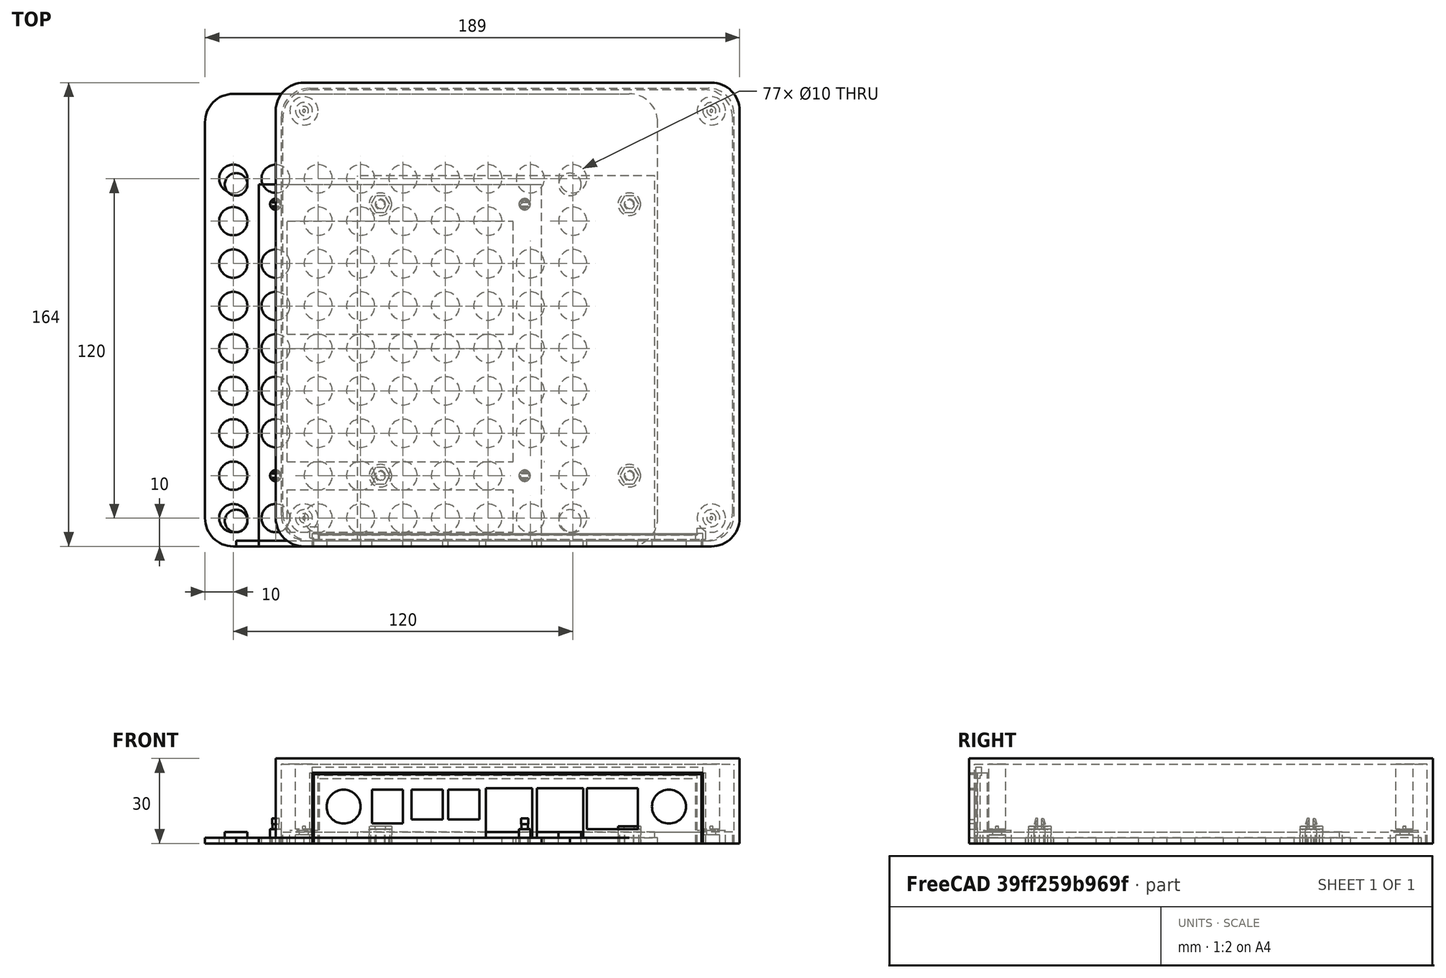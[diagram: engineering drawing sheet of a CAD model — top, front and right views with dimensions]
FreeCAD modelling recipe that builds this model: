
FCSTD DOCUMENT  (FreeCAD 0.16R6712 (Git))
Label: simple-case
License: All rights reserved
LicenseURL: http://en.wikipedia.org/wiki/All_rights_reserved
objects: Part::Fuse×53, Part::Cylinder×48, Part::Box×41, Part::Cut×27, PartDesign::Fillet×18, Part::FeaturePython×9, Part::Cone×4, Part::MultiCommon×4, Mesh::Feature×1, Sketcher::SketchObject×1, PartDesign::Pad×1
note: 207 computed .brp shape members not serialized (recipe doc carries the construction recipe); baked Part::Feature solids carry a one-line shape summary decoded from their .brp

FEATURE [PartDesign::Fillet] Fillet003
  Radius = 10
FEATURE [PartDesign::Fillet] Fillet007
  Placement = pos=(2,2,2) rot=(0,0,1;0rad)
  Radius = 9
FEATURE [Part::Cut] Cut
  Base = -> Fillet003
  Placement = pos=(-25,0,0) rot=(0,0,1;0rad)
  Tool = -> Fillet007
FEATURE [Part::Box] Box002  label="Ethernet"
  Height = 14.5
  Length = 18
  Placement = pos=(-1,0,-0.5) rot=(0,0,1;0rad)
  Width = 14.5
FEATURE [Part::Box] Box003  label="USB1"
  Height = 17.5
  Length = 16.4
  Placement = pos=(18.3,0,-0.5) rot=(0,0,1;0rad)
  Width = 10
FEATURE [Part::Box] Box004  label="USB2"
  Height = 17.5
  Length = 16.4
  Placement = pos=(36.3,0,-0.5) rot=(0,0,1;0rad)
  Width = 10
FEATURE [Part::Box] Box005  label="SPDIF1"
  Height = 10.5
  Length = 11
  Placement = pos=(55,0,0) rot=(0,0,1;0rad)
  Width = 10
FEATURE [Part::Box] Box006  label="SPDIF2"
  Height = 10.5
  Length = 11
  Placement = pos=(68,0,0) rot=(0,0,1;0rad)
  Width = 10
FEATURE [Part::Box] Box007  label="Power"
  Height = 12
  Length = 11
  Placement = pos=(82,0,0) rot=(0,0,1;0rad)
  Width = 10
FEATURE [Part::Fuse] Fusion
  Base = -> Box002
  Tool = -> Box003
FEATURE [Part::Fuse] Fusion001
  Base = -> Box007
  Tool = -> Fusion
FEATURE [Part::Fuse] Fusion002
  Base = -> Box006
  Tool = -> Fusion001
FEATURE [Part::Fuse] Fusion003
  Base = -> Box005
  Tool = -> Fusion002
FEATURE [Part::Fuse] Fusion004  label="Cutouts"
  Base = -> Box004
  Placement = pos=(90,-2,17) rot=(0,1,0;3.14159rad)
  Tool = -> Fusion003
FEATURE [Part::Cylinder] Cylinder  label="Zylinder"
  Angle = 360
  Height = 2
  Radius = 2
FEATURE [Part::Cylinder] Cylinder001  label="Zylinder001"
  Angle = 360
  Height = 3.8
  Radius = 1.3
FEATURE [Part::Cone] Cone  label="Kegel"
  Angle = 360
  Height = 2
  Placement = pos=(0,0,3.8) rot=(0,0,1;0rad)
  Radius1 = 2
  Radius2 = 1.4
FEATURE [Part::Box] Box008  label="Würfel008"
  Height = 4
  Length = 2.6
  Placement = pos=(-1.3,-5,3) rot=(0,0,1;0rad)
  Width = 10
FEATURE [Part::MultiCommon] Common
  Shapes = -> [Cone,Box008]
FEATURE [Part::Fuse] Fusion005
  Base = -> Cylinder
  Tool = -> Cylinder001
FEATURE [Part::Fuse] Fusion006
  Base = -> Common
  Tool = -> Fusion005
FEATURE [Part::Box] Box009  label="Würfel009"
  Height = 10
  Length = 10
  Placement = pos=(-3,-0.7,2) rot=(0,0,1;0rad)
  Width = 1.4
FEATURE [Part::Cut] Cut001
  Base = -> Fusion006
  Placement = pos=(0,23,0) rot=(0,0,1;0rad)
  Tool = -> Box009
FEATURE [Part::Cylinder] Cylinder002  label="Zylinder002"
  Angle = 360
  Height = 2
  Radius = 2
FEATURE [Part::Cylinder] Cylinder003  label="Zylinder003"
  Angle = 360
  Height = 3.8
  Radius = 1.3
FEATURE [Part::Cone] Cone001  label="Kegel001"
  Angle = 360
  Height = 2
  Placement = pos=(0,0,3.8) rot=(0,0,1;0rad)
  Radius1 = 2
  Radius2 = 1.4
FEATURE [Part::Box] Box010  label="Würfel010"
  Height = 4
  Length = 2.6
  Placement = pos=(-1.3,-5,3) rot=(0,0,1;0rad)
  Width = 10
FEATURE [Part::MultiCommon] Common001
  Shapes = -> [Cone001,Box010]
FEATURE [Part::Fuse] Fusion007
  Base = -> Cylinder002
  Tool = -> Cylinder003
FEATURE [Part::Fuse] Fusion008
  Base = -> Common001
  Tool = -> Fusion007
FEATURE [Part::Box] Box011  label="Würfel011"
  Height = 10
  Length = 10
  Placement = pos=(-3,-0.7,2) rot=(0,0,1;0rad)
  Width = 1.4
FEATURE [Part::Cut] Cut002
  Base = -> Fusion008
  Placement = pos=(0,119,0) rot=(0,0,1;0rad)
  Tool = -> Box011
FEATURE [Part::Cylinder] Cylinder004  label="Zylinder004"
  Angle = 360
  Height = 2
  Radius = 2
FEATURE [Part::Cylinder] Cylinder005  label="Zylinder005"
  Angle = 360
  Height = 3.8
  Radius = 1.3
FEATURE [Part::Cone] Cone002  label="Kegel002"
  Angle = 360
  Height = 2
  Placement = pos=(0,0,3.8) rot=(0,0,1;0rad)
  Radius1 = 2
  Radius2 = 1.4
FEATURE [Part::Box] Box012  label="Würfel012"
  Height = 4
  Length = 2.6
  Placement = pos=(-1.3,-5,3) rot=(0,0,1;0rad)
  Width = 10
FEATURE [Part::MultiCommon] Common002
  Shapes = -> [Cone002,Box012]
FEATURE [Part::Fuse] Fusion009
  Base = -> Cylinder004
  Tool = -> Cylinder005
FEATURE [Part::Fuse] Fusion010
  Base = -> Common002
  Tool = -> Fusion009
FEATURE [Part::Box] Box013  label="Würfel013"
  Height = 10
  Length = 10
  Placement = pos=(-3,-0.7,2) rot=(0,0,1;0rad)
  Width = 1.4
FEATURE [Part::Cut] Cut003
  Base = -> Fusion010
  Placement = pos=(88,23,0) rot=(0,0,1;0rad)
  Tool = -> Box013
FEATURE [Part::Cylinder] Cylinder006  label="Zylinder006"
  Angle = 360
  Height = 2
  Radius = 2
FEATURE [Part::Cylinder] Cylinder007  label="Zylinder007"
  Angle = 360
  Height = 3.8
  Radius = 1.3
FEATURE [Part::Cone] Cone003  label="Kegel003"
  Angle = 360
  Height = 2
  Placement = pos=(0,0,3.8) rot=(0,0,1;0rad)
  Radius1 = 2
  Radius2 = 1.4
FEATURE [Part::Box] Box014  label="Würfel014"
  Height = 4
  Length = 2.6
  Placement = pos=(-1.3,-5,3) rot=(0,0,1;0rad)
  Width = 10
FEATURE [Part::MultiCommon] Common003
  Shapes = -> [Cone003,Box014]
FEATURE [Part::Fuse] Fusion011
  Base = -> Cylinder006
  Tool = -> Cylinder007
FEATURE [Part::Fuse] Fusion012
  Base = -> Common003
  Tool = -> Fusion011
FEATURE [Part::Box] Box015  label="Würfel015"
  Height = 10
  Length = 10
  Placement = pos=(-3,-0.7,2) rot=(0,0,1;0rad)
  Width = 1.4
FEATURE [Part::Cut] Cut004
  Base = -> Fusion012
  Placement = pos=(88,119,0) rot=(0,0,1;0rad)
  Tool = -> Box015
FEATURE [Part::Fuse] Fusion013
  Base = -> Cut001
  Tool = -> Cut002
FEATURE [Part::Fuse] Fusion014
  Base = -> Cut003
  Tool = -> Cut004
FEATURE [Part::Fuse] Fusion015  label="Standoffs"
  Base = -> Fusion013
  Placement = pos=(0,0,3) rot=(0,0,1;0rad)
  Tool = -> Fusion014
FEATURE [Part::Cylinder] Cylinder008  label="Zylinder008"
  Angle = 360
  Height = 3
  Placement = pos=(88,23,0) rot=(0,0,1;0rad)
  Radius = 2
FEATURE [Part::Cylinder] Cylinder009  label="Zylinder009"
  Angle = 360
  Height = 3
  Placement = pos=(88,119,0) rot=(0,0,1;0rad)
  Radius = 2
FEATURE [Part::Cylinder] Cylinder010  label="Zylinder010"
  Angle = 360
  Height = 3
  Placement = pos=(0,23,0) rot=(0,0,1;0rad)
  Radius = 2
FEATURE [Part::Cylinder] Cylinder011  label="Zylinder011"
  Angle = 360
  Height = 3
  Placement = pos=(0,119,0) rot=(0,0,1;0rad)
  Radius = 2
FEATURE [Part::Box] Box017  label="Back_Full"
  Height = 22.5
  Length = 137
  Placement = pos=(-23.5,0,0) rot=(0,0,1;0rad)
  Width = 2
FEATURE [Part::Fuse] Fusion016
  Base = -> Cylinder008
  Tool = -> Cylinder009
FEATURE [Part::Fuse] Fusion017
  Base = -> Cylinder010
  Tool = -> Cylinder011
FEATURE [Part::Fuse] Fusion018
  Base = -> Fusion016
  Tool = -> Fusion017
FEATURE [Part::Fuse] Fusion019  label="LongStandoffs"
  Base = -> Fusion015
  Placement = pos=(0,2,0) rot=(0,0,1;0rad)
  Tool = -> Fusion018
FEATURE [Part::Cut] Cut005  label="Backplane"
  Base = -> Box017
  Placement = pos=(0,0,2) rot=(0,0,1;0rad)
  Tool = -> Fusion004
FEATURE [Mesh::Feature] beocreate_board  label="beocreate-board"
  Placement = pos=(91,125,6) rot=(0,0,1;3.14159rad)
FEATURE [Part::Cylinder] Cylinder012  label="Zylinder012"
  Angle = 360
  Height = 4
  Placement = pos=(-14,9,0) rot=(0,0,1;0rad)
  Radius = 4
FEATURE [Part::Cylinder] Cylinder013  label="Zylinder013"
  Angle = 360
  Height = 4
  Placement = pos=(-14,128,0) rot=(0,0,1;0rad)
  Radius = 4
FEATURE [Part::Cylinder] Cylinder014  label="Zylinder014"
  Angle = 360
  Height = 4
  Placement = pos=(104,9,0) rot=(0,0,1;0rad)
  Radius = 4
FEATURE [Part::Cylinder] Cylinder015  label="Zylinder015"
  Angle = 360
  Height = 4
  Placement = pos=(104,128,0) rot=(0,0,1;0rad)
  Radius = 4
FEATURE [Part::Fuse] Fusion020
  Base = -> Cylinder012
  Tool = -> Cylinder013
FEATURE [Part::Fuse] Fusion021
  Base = -> Cylinder014
  Tool = -> Cylinder015
FEATURE [Part::Box] Box018  label="Würfel017"
  Height = 2
  Length = 100
  Placement = pos=(-6,0,0) rot=(0,0,1;0rad)
  Width = 128
FEATURE [Part::Box] Box019  label="Würfel018"
  Height = 2
  Length = 80
  Placement = pos=(4,75,0) rot=(0,0,1;0rad)
  Width = 40
FEATURE [Part::Box] Box020  label="Würfel019"
  Height = 2
  Length = 80
  Placement = pos=(4,30,0) rot=(0,0,1;0rad)
  Width = 40
FEATURE [Part::Box] Box021  label="Würfel020"
  Height = 2
  Length = 80
  Placement = pos=(4,5,0) rot=(0,0,1;0rad)
  Width = 15
FEATURE [Part::Fuse] Fusion022
  Base = -> Box019
  Tool = -> Box020
FEATURE [Part::Fuse] Fusion023
  Base = -> Box021
  Tool = -> Fusion022
FEATURE [Part::Cut] Cut006
  Base = -> Box018
  Tool = -> Fusion023
FEATURE [Part::Cylinder] Cylinder016  label="Zylinder016"
  Angle = 360
  Height = 5
  Radius = 4
FEATURE [Part::Cylinder] Cylinder017  label="Zylinder017"
  Angle = 360
  Height = 10
  Radius = 1.5
FEATURE [Part::Cut] Cut007  label="Noppe1"
  Base = -> Cylinder016
  Placement = pos=(0,25,2) rot=(0,0,1;0rad)
  Tool = -> Cylinder017
FEATURE [Part::Cylinder] Cylinder018  label="Zylinder018"
  Angle = 360
  Height = 5
  Radius = 4
FEATURE [Part::Cylinder] Cylinder019  label="Zylinder019"
  Angle = 360
  Height = 10
  Radius = 1.5
FEATURE [Part::Cut] Cut008  label="Noppe002"
  Base = -> Cylinder018
  Placement = pos=(0,121,2) rot=(0,0,1;0rad)
  Tool = -> Cylinder019
FEATURE [Part::Cylinder] Cylinder020  label="Zylinder020"
  Angle = 360
  Height = 5
  Radius = 4
FEATURE [Part::Cylinder] Cylinder021  label="Zylinder021"
  Angle = 360
  Height = 10
  Radius = 1.5
FEATURE [Part::Cut] Cut009  label="Noppe003"
  Base = -> Cylinder020
  Placement = pos=(88,121,2) rot=(0,0,1;0rad)
  Tool = -> Cylinder021
FEATURE [Part::Cylinder] Cylinder022  label="Zylinder022"
  Angle = 360
  Height = 5
  Radius = 4
FEATURE [Part::Cylinder] Cylinder023  label="Zylinder023"
  Angle = 360
  Height = 10
  Radius = 1.5
FEATURE [Part::Cut] Cut010  label="Noppe004"
  Base = -> Cylinder022
  Placement = pos=(88,25,2) rot=(0,0,1;0rad)
  Tool = -> Cylinder023
FEATURE [Part::Cylinder] Cylinder024  label="Zylinder024"
  Angle = 360
  Height = 10
  Placement = pos=(0,25,0) rot=(0,0,1;0rad)
  Radius = 1.5
FEATURE [Part::Cylinder] Cylinder025  label="Zylinder025"
  Angle = 360
  Height = 10
  Placement = pos=(88,25,0) rot=(0,0,1;0rad)
  Radius = 1.5
FEATURE [Part::Cylinder] Cylinder026  label="Zylinder026"
  Angle = 360
  Height = 10
  Placement = pos=(0,121,0) rot=(0,0,1;0rad)
  Radius = 1.5
FEATURE [Part::Cylinder] Cylinder027  label="Zylinder027"
  Angle = 360
  Height = 10
  Placement = pos=(88,121,0) rot=(0,0,1;0rad)
  Radius = 1.5
FEATURE [Part::Fuse] Fusion024
  Base = -> Cylinder024
  Tool = -> Cylinder025
FEATURE [Part::Fuse] Fusion025
  Base = -> Cylinder026
  Tool = -> Cylinder027
FEATURE [Part::Fuse] Fusion026
  Base = -> Fusion024
  Tool = -> Fusion025
FEATURE [Part::Cut] Cut011
  Base = -> Cut006
  Tool = -> Fusion026
FEATURE [Part::Box] Box022  label="Würfel021"
  Height = 2
  Length = 118
  Placement = pos=(-14,0,0) rot=(0,0,1;0rad)
  Width = 2
FEATURE [Part::Fuse] Fusion027
  Base = -> Cut007
  Tool = -> Cut008
FEATURE [Part::Fuse] Fusion028
  Base = -> Cut009
  Tool = -> Cut010
FEATURE [Part::Fuse] Fusion029  label="Noppen"
  Base = -> Fusion027
  Placement = pos=(37,0,-2) rot=(0,0,1;0rad)
  Tool = -> Fusion028
FEATURE [Part::Box] Box023  label="Würfel022"
  Height = 10
  Length = 10
  Placement = pos=(-5,20,0) rot=(0,0,1;0rad)
  Width = 10
FEATURE [Part::Box] Box024  label="Würfel023"
  Height = 10
  Length = 10
  Placement = pos=(-5,115,0) rot=(0,0,1;0rad)
  Width = 10
FEATURE [Part::Box] Box025  label="Würfel024"
  Height = 10
  Length = 10
  Placement = pos=(85,20,0) rot=(0,0,1;0rad)
  Width = 10
FEATURE [Part::Box] Box026  label="Würfel025"
  Height = 10
  Length = 10
  Placement = pos=(83,115,0) rot=(0,0,1;0rad)
  Width = 10
FEATURE [Part::Fuse] Fusion030
  Base = -> Box023
  Tool = -> Box024
FEATURE [Part::Fuse] Fusion031
  Base = -> Box025
  Tool = -> Box026
FEATURE [Part::Fuse] Fusion032
  Base = -> Fusion030
  Tool = -> Fusion031
FEATURE [Part::Cut] Cut012
  Base = -> Cut
  Tool = -> Fusion032
FEATURE [Part::Cylinder] Cylinder028  label="Zylinder028"
  Angle = 360
  Height = 10
  Radius = 5
FEATURE [Part::FeaturePython] Array  # Draft array (typed FeaturePython)
  Angle = 360
  ArrayType = 0
  Axis = (0,0,1)
  Base = -> Cylinder028
  Center = (0,0,0)
  Fuse = false
  IntervalAxis = (0,0,0)
  IntervalX = (15,0,0)
  IntervalY = (0,15,0)
  IntervalZ = (0,0,0)
  NumberPolar = 1
  NumberX = 9
  NumberY = 9
  NumberZ = 1
  Placement = pos=(-15,10,0) rot=(0,0,1;0rad)
FEATURE [Part::Box] Box027  label="Würfel026"
  Height = 2
  Length = 100
  Placement = pos=(-6,0,0) rot=(0,0,1;0rad)
  Width = 128
FEATURE [Part::Box] Box028  label="Würfel027"
  Height = 2
  Length = 80
  Placement = pos=(4,75,0) rot=(0,0,1;0rad)
  Width = 40
FEATURE [Part::Box] Box029  label="Würfel028"
  Height = 2
  Length = 80
  Placement = pos=(4,30,0) rot=(0,0,1;0rad)
  Width = 40
FEATURE [Part::Box] Box030  label="Würfel029"
  Height = 2
  Length = 80
  Placement = pos=(4,5,0) rot=(0,0,1;0rad)
  Width = 15
FEATURE [Part::Fuse] Fusion033
  Base = -> Box028
  Tool = -> Box029
FEATURE [Part::Fuse] Fusion034
  Base = -> Box030
  Tool = -> Fusion033
FEATURE [Part::Cut] Cut013
  Base = -> Box027
  Tool = -> Fusion034
FEATURE [Part::Cylinder] Cylinder029  label="Zylinder029"
  Angle = 360
  Height = 10
  Placement = pos=(0,25,0) rot=(0,0,1;0rad)
  Radius = 1.5
FEATURE [Part::Cylinder] Cylinder030  label="Zylinder030"
  Angle = 360
  Height = 10
  Placement = pos=(88,25,0) rot=(0,0,1;0rad)
  Radius = 1.5
FEATURE [Part::Cylinder] Cylinder031  label="Zylinder031"
  Angle = 360
  Height = 10
  Placement = pos=(0,121,0) rot=(0,0,1;0rad)
  Radius = 1.5
FEATURE [Part::Cylinder] Cylinder032  label="Zylinder032"
  Angle = 360
  Height = 10
  Placement = pos=(88,121,0) rot=(0,0,1;0rad)
  Radius = 1.5
FEATURE [Part::Fuse] Fusion035
  Base = -> Cylinder029
  Tool = -> Cylinder030
FEATURE [Part::Fuse] Fusion036
  Base = -> Cylinder031
  Tool = -> Cylinder032
FEATURE [Part::Fuse] Fusion037
  Base = -> Fusion035
  Tool = -> Fusion036
FEATURE [Part::Cut] Cut014
  Base = -> Cut013
  Tool = -> Fusion037
FEATURE [Part::Fuse] Fusion038
  Base = -> Cut012
  Tool = -> Cut014
FEATURE [Part::Cut] Cut015
  Base = -> Fusion038
  Tool = -> Array
FEATURE [Part::Cylinder] Cylinder033  label="Zylinder033"
  Angle = 360
  Height = 2
  Placement = pos=(0,25,0) rot=(0,0,1;0rad)
  Radius = 7
FEATURE [Part::Cylinder] Cylinder034  label="Zylinder034"
  Angle = 360
  Height = 2
  Placement = pos=(90,25,0) rot=(0,0,1;0rad)
  Radius = 7
FEATURE [Part::Cylinder] Cylinder035  label="Zylinder035"
  Angle = 360
  Height = 2
  Placement = pos=(90,115,0) rot=(0,0,1;0rad)
  Radius = 7
FEATURE [Part::Cylinder] Cylinder036  label="Zylinder036"
  Angle = 360
  Height = 2
  Placement = pos=(0,115,0) rot=(0,0,1;0rad)
  Radius = 7
FEATURE [Part::Fuse] Fusion039
  Base = -> Cylinder033
  Tool = -> Cylinder034
FEATURE [Part::Fuse] Fusion040
  Base = -> Cylinder035
  Tool = -> Cylinder036
FEATURE [Part::Fuse] Fusion041
  Base = -> Fusion039
  Tool = -> Fusion040
FEATURE [Part::Fuse] Fusion042  label="Boden"
  Base = -> Cut015
  Tool = -> Fusion041
FEATURE [Part::Box] Box031  label="Würfel030"
  Height = 30
  Length = 164
  Width = 164
FEATURE [PartDesign::Fillet] Fillet012
  Base = -> Box031 [Edge1]
  Radius = 10
FEATURE [PartDesign::Fillet] Fillet013
  Base = -> Fillet012 [Edge15]
  Radius = 10
FEATURE [PartDesign::Fillet] Fillet014
  Base = -> Fillet013 [Edge14]
  Radius = 10
FEATURE [Part::Box] Box032  label="Würfel031"
  Height = 28
  Length = 160
  Placement = pos=(2,2,0) rot=(0,0,1;0rad)
  Width = 160
FEATURE [PartDesign::Fillet] Fillet016
  Base = -> Box032 [Edge1]
  Placement = pos=(2,2,0) rot=(0,0,1;0rad)
  Radius = 9
FEATURE [PartDesign::Fillet] Fillet017
  Base = -> Fillet016 [Edge15]
  Placement = pos=(2,2,0) rot=(0,0,1;0rad)
  Radius = 9
FEATURE [PartDesign::Fillet] Fillet018
  Base = -> Fillet017 [Edge14]
  Placement = pos=(2,2,0) rot=(0,0,1;0rad)
  Radius = 9
FEATURE [PartDesign::Fillet] Fillet019
  Base = -> Fillet014 [Edge16]
  Radius = 10
FEATURE [PartDesign::Fillet] Fillet020
  Base = -> Fillet018 [Edge16]
  Placement = pos=(2,2,0) rot=(0,0,1;0rad)
  Radius = 10
FEATURE [Part::Cut] Cut016  label="Deckel1"
  Base = -> Fillet019
  Tool = -> Fillet020
FEATURE [Part::Box] Box033  label="Würfel032"
  Height = 25
  Length = 138
  Placement = pos=(13,0,0) rot=(0,0,1;0rad)
  Width = 2
FEATURE [Part::Cut] Cut017
  Base = -> Cut016
  Tool = -> Box033
FEATURE [Part::Cylinder] Cylinder037  label="Zylinder037"
  Angle = 360
  Height = 25
  Placement = pos=(0,0,5) rot=(0,0,1;0rad)
  Radius = 3
FEATURE [Part::Cylinder] Cylinder038  label="Zylinder038"
  Angle = 360
  Height = 6
  Radius = 0.5
FEATURE [Part::Cut] Cut018
  Base = -> Cylinder037
  Placement = pos=(10,10,0) rot=(0,0,1;0rad)
  Tool = -> Cylinder038
FEATURE [Part::FeaturePython] Array001  # Draft array (typed FeaturePython)
  Angle = 360
  ArrayType = 0
  Axis = (0,0,1)
  Base = -> Cut018
  Center = (0,0,0)
  Fuse = false
  IntervalAxis = (0,0,0)
  IntervalX = (144,0,0)
  IntervalY = (0,144,0)
  IntervalZ = (0,0,0)
  NumberPolar = 1
  NumberX = 2
  NumberY = 2
  NumberZ = 1
FEATURE [Part::Fuse] Fusion043  label="Deckel"
  Base = -> Cut017
  Tool = -> Array001
FEATURE [Part::Cylinder] Cylinder039  label="Zylinder039"
  Angle = 360
  Height = 10
  Placement = pos=(-13,5,13) rot=(1,0,0;1.5708rad)
  Radius = 6
FEATURE [Part::FeaturePython] Array002  # Draft array (typed FeaturePython)
  Angle = 360
  ArrayType = 0
  Axis = (0,0,1)
  Base = -> Cylinder039
  Center = (0,0,0)
  Fuse = false
  IntervalAxis = (0,0,0)
  IntervalX = (1,0,0)
  IntervalY = (0,1,0)
  IntervalZ = (115,0,0)
  NumberPolar = 1
  NumberX = 1
  NumberY = 1
  NumberZ = 2
FEATURE [Part::Cut] Cut019  label="Backplane2"
  Base = -> Cut005
  Placement = pos=(37,0,0) rot=(0,0,1;0rad)
  Tool = -> Array002
FEATURE [Part::Box] Box  label="Würfel"
  Height = 2
  Length = 159
  Placement = pos=(2.5,2,0) rot=(0,0,1;0rad)
  Width = 159.5
FEATURE [PartDesign::Fillet] Fillet
  Base = -> Box [Edge5]
  Placement = pos=(2.5,2,0) rot=(0,0,1;0rad)
  Radius = 10
FEATURE [PartDesign::Fillet] Fillet021
  Base = -> Fillet [Edge3]
  Placement = pos=(2.5,2,0) rot=(0,0,1;0rad)
  Radius = 10
FEATURE [PartDesign::Fillet] Fillet022
  Base = -> Fillet021 [Edge18]
  Placement = pos=(2.5,2,0) rot=(0,0,1;0rad)
  Radius = 10
FEATURE [PartDesign::Fillet] Fillet023  label="Boden1"
  Base = -> Fillet022 [Edge15]
  Placement = pos=(2.5,2,0) rot=(0,0,1;0rad)
  Radius = 10
FEATURE [Part::Box] Box034  label="Würfel033"
  Height = 2
  Length = 137
  Placement = pos=(13.5,0,0) rot=(0,0,1;0rad)
  Width = 2
FEATURE [Part::Fuse] Fusion044  label="Backplane3"
  Base = -> Cut019
  Tool = -> Box034
FEATURE [Sketcher::SketchObject] Sketch
  Placement = pos=(37,25,0) rot=(0,0,1;0rad)
  sketch-geometry (33):
    g0: LineSegment StartX=-1.67432 StartY=-2.9 StartZ=0 EndX=1.67432 EndY=-2.9 EndZ=0
    g1: LineSegment StartX=1.67432 StartY=-2.9 StartZ=0 EndX=3.34863 EndY=0 EndZ=0
    g2: LineSegment StartX=3.34863 StartY=0 StartZ=0 EndX=1.67432 EndY=2.9 EndZ=0
    g3: LineSegment StartX=1.67432 StartY=2.9 StartZ=0 EndX=-1.67432 EndY=2.9 EndZ=0
    g4: LineSegment StartX=-1.67432 StartY=2.9 StartZ=0 EndX=-3.34863 EndY=0 EndZ=0
    g5: LineSegment StartX=-3.34863 StartY=0 StartZ=0 EndX=-1.67432 EndY=-2.9 EndZ=0
    g6: Circle [constr] CenterX=0 CenterY=0 CenterZ=0 NormalX=0 NormalY=0 NormalZ=1 Radius=3.34863
    g7: LineSegment StartX=3.34863 StartY=96 StartZ=0 EndX=1.67432 EndY=98.9 EndZ=0
    g8: LineSegment StartX=1.67432 StartY=98.9 StartZ=0 EndX=-1.67432 EndY=98.9 EndZ=0
    g9: LineSegment StartX=-1.67432 StartY=98.9 StartZ=0 EndX=-3.34863 EndY=96 EndZ=0
    g10: LineSegment StartX=-3.34863 StartY=96 StartZ=0 EndX=-1.67432 EndY=93.1 EndZ=0
    g11: LineSegment StartX=-1.67432 StartY=93.1 StartZ=0 EndX=1.67432 EndY=93.1 EndZ=0
    g12: LineSegment StartX=1.67432 StartY=93.1 StartZ=0 EndX=3.34863 EndY=96 EndZ=0
    g13: Circle [constr] CenterX=0 CenterY=96 CenterZ=0 NormalX=0 NormalY=0 NormalZ=1 Radius=3.34863
    g14: LineSegment StartX=91.3486 StartY=96 StartZ=0 EndX=89.6743 EndY=98.9 EndZ=0
    g15: LineSegment StartX=89.6743 StartY=98.9 StartZ=0 EndX=86.3257 EndY=98.9 EndZ=0
    g16: LineSegment StartX=86.3257 StartY=98.9 StartZ=0 EndX=84.6514 EndY=96 EndZ=0
    g17: LineSegment StartX=84.6514 StartY=96 StartZ=0 EndX=86.3257 EndY=93.1 EndZ=0
    g18: LineSegment StartX=86.3257 StartY=93.1 StartZ=0 EndX=89.6743 EndY=93.1 EndZ=0
    g19: LineSegment StartX=89.6743 StartY=93.1 StartZ=0 EndX=91.3486 EndY=96 EndZ=0
    g20: Circle [constr] CenterX=88 CenterY=96 CenterZ=0 NormalX=0 NormalY=0 NormalZ=1 Radius=3.34863
    g21: LineSegment StartX=89.6743 StartY=-2.9 StartZ=0 EndX=91.3486 EndY=0 EndZ=0
    g22: LineSegment StartX=91.3486 StartY=0 StartZ=0 EndX=89.6743 EndY=2.9 EndZ=0
    g23: LineSegment StartX=89.6743 StartY=2.9 StartZ=0 EndX=86.3257 EndY=2.9 EndZ=0
    g24: LineSegment StartX=86.3257 StartY=2.9 StartZ=0 EndX=84.6514 EndY=0 EndZ=0
    g25: LineSegment StartX=84.6514 StartY=0 StartZ=0 EndX=86.3257 EndY=-2.9 EndZ=0
    g26: LineSegment StartX=86.3257 StartY=-2.9 StartZ=0 EndX=89.6743 EndY=-2.9 EndZ=0
    g27: Circle [constr] CenterX=88 CenterY=0 CenterZ=0 NormalX=0 NormalY=0 NormalZ=1 Radius=3.34863
    g28: Circle CenterX=0 CenterY=0 CenterZ=0 NormalX=0 NormalY=0 NormalZ=1 Radius=4
    g29: Circle CenterX=-4 CenterY=0 CenterZ=0 NormalX=0 NormalY=0 NormalZ=1 Radius=0
    g30: Circle CenterX=0 CenterY=96 CenterZ=0 NormalX=0 NormalY=0 NormalZ=1 Radius=4
    g31: Circle CenterX=88 CenterY=96 CenterZ=0 NormalX=0 NormalY=0 NormalZ=1 Radius=4
    g32: Circle CenterX=88 CenterY=0 CenterZ=0 NormalX=0 NormalY=0 NormalZ=1 Radius=4
  constraints (77):
    c: Coincident(g0,g1)
    c: Coincident(g1,g2)
    c: Coincident(g2,g3)
    c: Coincident(g3,g4)
    c: Coincident(g4,g5)
    c: Coincident(g5,g0)
    c: Equal(g0, g1-g5) x5
    c: PointOnObject(g0,g6)
    c: PointOnObject(g1,g6)
    c: PointOnObject(g2,g6)
    c: PointOnObject(g3,g6)
    c: PointOnObject(g4,g6)
    c: PointOnObject(g5,g6)
    c: Coincident(g6,g-1)
    c: Horizontal(g3)
    c: DistanceY(g0,g3) = 5.8
    c: Coincident(g7,g8)
    c: Coincident(g8,g9)
    c: Coincident(g9,g10)
    c: Coincident(g10,g11)
    c: Coincident(g11,g12)
    c: Coincident(g12,g7)
    c: Equal(g7, g8-g12) x5
    c: PointOnObject(g7,g13)
    c: PointOnObject(g8,g13)
    c: PointOnObject(g9,g13)
    c: PointOnObject(g10,g13)
    c: PointOnObject(g11,g13)
    c: PointOnObject(g12,g13)
    c: Coincident(g14,g15)
    c: Coincident(g15,g16)
    c: Coincident(g16,g17)
    c: Coincident(g17,g18)
    c: Coincident(g18,g19)
    c: Coincident(g19,g14)
    c: Equal(g14, g15-g19) x5
    c: PointOnObject(g14,g20)
    c: PointOnObject(g15,g20)
    c: PointOnObject(g16,g20)
    c: PointOnObject(g17,g20)
    c: PointOnObject(g18,g20)
    c: PointOnObject(g19,g20)
    c: Coincident(g21,g22)
    c: Coincident(g22,g23)
    c: Coincident(g23,g24)
    c: Coincident(g24,g25)
    c: Coincident(g25,g26)
    c: Coincident(g26,g21)
    c: Equal(g21, g22-g26) x5
    c: PointOnObject(g21,g27)
    c: PointOnObject(g22,g27)
    c: PointOnObject(g23,g27)
    c: PointOnObject(g24,g27)
    c: PointOnObject(g25,g27)
    c: PointOnObject(g26,g27)
    c: Horizontal(g8)
    c: Horizontal(g15)
    c: Horizontal(g23)
    c: DistanceY(g15,g7) = 0
    c: DistanceY(g0,g25) = 0
    c: DistanceX(g3,g8) = 0
    c: DistanceY(g17,g11) = 0
    c: DistanceX(g17,g23) = 0
    c: DistanceY(g23,g2) = 0
    c: Coincident(g28,g-1)
    c: PointOnObject(g29,g28)
    c: Coincident(g30,g13)
    c: Coincident(g20,g31)
    c: Coincident(g32,g27)
    c: DistanceX(g-1,g27) = 88
    c: DistanceY(g-1,g13) = 96
    c: DistanceX(g11,g2) = 0
    c: Radius(g28) = 4
    c: DistanceY(g-1,g29) = 0
    c: Radius(g30) = 4
    c: Radius(g31) = 4
    c: Radius(g32) = 4
FEATURE [PartDesign::Pad] Pad
  Length = 6
  Length2 = 100
  Placement = pos=(37,25,0) rot=(0,0,1;0rad)
  Sketch = -> Sketch
  Type = 0
FEATURE [Part::Cylinder] Cylinder040  label="Zylinder040"
  Angle = 360
  Height = 1
  Placement = pos=(37,25,5) rot=(0,0,1;0rad)
  Radius = 4
FEATURE [Part::FeaturePython] Array003  # Draft array (typed FeaturePython)
  Angle = 360
  ArrayType = 0
  Axis = (0,0,1)
  Base = -> Cylinder040
  Center = (0,0,0)
  Fuse = false
  IntervalAxis = (0,0,0)
  IntervalX = (88,0,0)
  IntervalY = (0,96,0)
  IntervalZ = (0,0,0)
  NumberPolar = 1
  NumberX = 2
  NumberY = 2
  NumberZ = 1
FEATURE [Part::Fuse] Fusion045
  Base = -> Pad
  Tool = -> Array003
FEATURE [Part::Cylinder] Cylinder041  label="Zylinder041"
  Angle = 360
  Height = 10
  Placement = pos=(37,25,0) rot=(0,0,1;0rad)
  Radius = 1.8
FEATURE [Part::FeaturePython] Array004  # Draft array (typed FeaturePython)
  Angle = 360
  ArrayType = 0
  Axis = (0,0,1)
  Base = -> Cylinder041
  Center = (0,0,0)
  Fuse = false
  IntervalAxis = (0,0,0)
  IntervalX = (88,0,0)
  IntervalY = (0,96,0)
  IntervalZ = (0,0,0)
  NumberPolar = 1
  NumberX = 2
  NumberY = 2
  NumberZ = 1
FEATURE [Part::Cut] Cut020  label="Standoffs001"
  Base = -> Fusion045
  Tool = -> Array004
FEATURE [Part::Cylinder] Cylinder042  label="Zylinder042"
  Angle = 360
  Height = 10
  Placement = pos=(37,25,0) rot=(0,0,1;0rad)
  Radius = 4
FEATURE [Part::FeaturePython] Array005  # Draft array (typed FeaturePython)
  Angle = 360
  ArrayType = 0
  Axis = (0,0,1)
  Base = -> Cylinder042
  Center = (0,0,0)
  Fuse = false
  IntervalAxis = (0,0,0)
  IntervalX = (88,0,0)
  IntervalY = (0,96,0)
  IntervalZ = (0,0,0)
  NumberPolar = 1
  NumberX = 2
  NumberY = 2
  NumberZ = 1
FEATURE [Part::Cut] Cut021  label="Boden2"
  Base = -> Fillet023
  Tool = -> Array005
FEATURE [Part::Box] Box035  label="Würfel034"
  Height = 25
  Length = 3
  Placement = pos=(12,3,0) rot=(0,0,1;0rad)
  Width = 4
FEATURE [Part::Box] Box036  label="Würfel035"
  Height = 25
  Length = 3
  Placement = pos=(149,2.5,0) rot=(0,0,1;0rad)
  Width = 4
FEATURE [Part::Fuse] Fusion046
  Base = -> Box035
  Tool = -> Box036
FEATURE [Part::Fuse] Fusion047  label="Backplane004"
  Base = -> Fusion044
  Tool = -> Fusion046
FEATURE [Part::Cylinder] Cylinder043  label="Zylinder043"
  Angle = 360
  Height = 4.5
  Radius = 5
FEATURE [Part::Cylinder] Cylinder044  label="Zylinder044"
  Angle = 360
  Height = 10
  Radius = 1.6
FEATURE [Part::Cut] Cut022
  Base = -> Cylinder043
  Tool = -> Cylinder044
FEATURE [Part::Cylinder] Cylinder045  label="Zylinder045"
  Angle = 360
  Height = 3
  Radius = 3
FEATURE [Part::Cut] Cut023
  Base = -> Cut022
  Tool = -> Cylinder045
FEATURE [Part::FeaturePython] Array006  label="Standoff1"  # Draft array (typed FeaturePython)
  Angle = 360
  ArrayType = 0
  Axis = (0,0,1)
  Base = -> Cut023
  Center = (0,0,0)
  Fuse = false
  IntervalAxis = (0,0,0)
  IntervalX = (144,0,0)
  IntervalY = (0,144,0)
  IntervalZ = (0,0,0)
  NumberPolar = 1
  NumberX = 2
  NumberY = 2
  NumberZ = 1
  Placement = pos=(10,10,0) rot=(0,0,1;0rad)
FEATURE [Part::Cylinder] Cylinder046  label="Zylinder046"
  Angle = 360
  Height = 10
  Placement = pos=(10,10,0) rot=(0,0,1;0rad)
  Radius = 3
FEATURE [Part::FeaturePython] Array007  # Draft array (typed FeaturePython)
  Angle = 360
  ArrayType = 0
  Axis = (0,0,1)
  Base = -> Cylinder046
  Center = (0,0,0)
  Fuse = false
  IntervalAxis = (0,0,0)
  IntervalX = (144,0,0)
  IntervalY = (0,144,0)
  IntervalZ = (0,0,0)
  NumberPolar = 1
  NumberX = 2
  NumberY = 2
  NumberZ = 1
FEATURE [Part::Cut] Cut024  label="Boden3"
  Base = -> Cut021
  Tool = -> Array007
FEATURE [Part::Box] Box037  label="Würfel036"
  Height = 3
  Length = 138
  Placement = pos=(13,2.5,24) rot=(0,0,1;0rad)
  Width = 2
FEATURE [Part::Box] Box038  label="Würfel037"
  Height = 25
  Length = 2
  Placement = pos=(13.5,2,0) rot=(0,0,1;0rad)
  Width = 2
FEATURE [Part::Box] Box039  label="Würfel038"
  Height = 25
  Length = 2
  Placement = pos=(148.5,2,0) rot=(0,0,1;0rad)
  Width = 2
FEATURE [Part::Box] Box040  label="Würfel039"
  Height = 2
  Length = 137
  Placement = pos=(13.5,2,23) rot=(0,0,1;0rad)
  Width = 2
FEATURE [Part::Fuse] Fusion048
  Base = -> Box038
  Tool = -> Box039
FEATURE [Part::Fuse] Fusion049
  Base = -> Box037
  Tool = -> Box040
FEATURE [Part::Fuse] Fusion050
  Base = -> Fusion048
  Tool = -> Fusion049
FEATURE [Part::Fuse] Fusion051  label="Backplane5"
  Base = -> Fusion047
  Tool = -> Fusion050
FEATURE [Part::Box] Box041  label="Würfel040"
  Height = 2
  Length = 159
  Placement = pos=(2.5,2,2) rot=(0,0,1;0rad)
  Width = 159.5
FEATURE [PartDesign::Fillet] Fillet024
  Base = -> Box041 [Edge5]
  Placement = pos=(2.5,2,2) rot=(0,0,1;0rad)
  Radius = 10
FEATURE [PartDesign::Fillet] Fillet025
  Base = -> Fillet024 [Edge3]
  Placement = pos=(2.5,2,2) rot=(0,0,1;0rad)
  Radius = 10
FEATURE [PartDesign::Fillet] Fillet026
  Base = -> Fillet025 [Edge18]
  Placement = pos=(2.5,2,2) rot=(0,0,1;0rad)
  Radius = 10
FEATURE [PartDesign::Fillet] Fillet027  label="Boden004"
  Base = -> Fillet026 [Edge15]
  Placement = pos=(2.5,2,2) rot=(0,0,1;0rad)
  Radius = 10
FEATURE [Part::Cylinder] Cylinder047  label="Zylinder047"
  Angle = 360
  Height = 10
  Placement = pos=(10,10,0) rot=(0,0,1;0rad)
  Radius = 3
FEATURE [Part::FeaturePython] Array008  # Draft array (typed FeaturePython)
  Angle = 360
  ArrayType = 0
  Axis = (0,0,1)
  Base = -> Cylinder047
  Center = (0,0,0)
  Fuse = false
  IntervalAxis = (0,0,0)
  IntervalX = (144,0,0)
  IntervalY = (0,144,0)
  IntervalZ = (0,0,0)
  NumberPolar = 1
  NumberX = 2
  NumberY = 2
  NumberZ = 1
FEATURE [Part::Cut] Cut025
  Base = -> Fillet027
  Tool = -> Array008
FEATURE [Part::Box] Box042  label="Würfel041"
  Height = 10
  Length = 105
  Placement = pos=(29,1,0) rot=(0,0,1;0rad)
  Width = 130
FEATURE [Part::Cut] Cut026
  Base = -> Cut025
  Tool = -> Box042
FEATURE [Part::Fuse] Fusion052  label="Boden4"
  Base = -> Cut024
  Tool = -> Cut026
